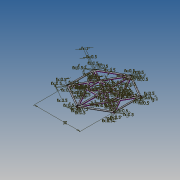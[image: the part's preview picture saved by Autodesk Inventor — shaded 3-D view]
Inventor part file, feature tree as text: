
AUTODESK INVENTOR PART (.ipt)
format: ipt  version: 2015 SP1 (Build 190203100, 203)  size: 1,105,920 bytes
history: native  units: mm
features: extrude x23, other x5, sketch x1, fillet x1, pattern_circular x1
ambient origin geometry x8: Origin, YZ Plane, XZ Plane, XY Plane, X Axis, Y Axis, Z Axis, Center Point
bodies: Solid1 (feature_tree), Solid3 (feature_tree), Solid4 (feature_tree), Solid5 (feature_tree), Solid6 (feature_tree), Solid7 (feature_tree), Solid8 (feature_tree), Solid9 (feature_tree), Solid11 (feature_tree), Solid12 (feature_tree), Solid13 (feature_tree), Solid14 (feature_tree), Solid16 (feature_tree), Solid17 (feature_tree), Solid18 (feature_tree), Solid19 (feature_tree), Solid20 (feature_tree), Solid21 (feature_tree), Solid22 (feature_tree), Solid23 (feature_tree), Solid24 (feature_tree), Solid25 (feature_tree), Solid26 (feature_tree), Solid27 (feature_tree), Solid28 (feature_tree), Solid29 (feature_tree), Solid30 (feature_tree), Solid31 (feature_tree)
feature tree (31):
  sketch  "Sketch1"  dims[d5=30.0mm d8=1.0mm d9=0.5mm d10=0.5mm d11=0.5mm d16=1.0mm d17=0.0mm d20=0.49mm d21=60.0mm d22=360.0deg d25=0.5mm d26=0.5mm d27=1.0mm d28=0.5mm d29=0.5mm d30=0.5mm d31=1.0mm d32=0.5mm d33=1.0mm d34=0.0mm d35=1.0mm d36=0.0mm d38=0.5mm d39=1.0mm d40=0.5mm d41=0.5mm d42=1.0mm d44=0.5mm d45=0.5mm d46=0.5mm d47=0.5mm d48=0.5mm d49=0.5mm d50=0.5mm d51=0.5mm d52=0.5mm d53=0.5mm d54=1.0mm d55=0.0mm d56=1.0mm d57=0.0mm d58=1.0mm d59=0.0mm d60=1.0mm d61=0.0mm d62=0.5mm d63=1.0mm d64=0.5mm d65=0.5mm d66=1.0mm d67=0.0mm d68=0.5mm d69=1.0mm d70=0.5mm d71=0.5mm d72=0.5mm d73=1.0mm d74=0.5mm d75=0.5mm d76=0.5mm d79=0.5mm d81=0.5mm d82=1.0mm d83=0.5mm d84=1.0mm d85=0.0mm d86=1.0mm d87=0.0mm d88=1.0mm d89=0.0mm d90=1.0mm d91=0.0mm d92=0.5mm d93=0.5mm d94=0.5mm d95=1.0mm d96=1.0mm d97=0.0mm d98=0.5mm d99=0.5mm d100=1.0mm d101=0.5mm d102=0.5mm d103=1.0mm d104=0.5mm d105=0.5mm d106=0.5mm d107=1.0mm d108=0.5mm d109=0.5mm d110=0.5mm d111=0.5mm d112=0.5mm d113=1.0mm d114=0.5mm d116=1.0mm d117=0.5mm d118=0.5mm d119=0.5mm d120=0.5mm d121=1.0mm d122=0.5mm d123=0.5mm d124=0.5mm d125=1.0mm d126=0.5mm d127=0.5mm d128=0.5mm d129=1.0mm d130=0.5mm d131=1.0mm d132=0.0mm d133=1.0mm d134=0.0mm d135=1.0mm d136=0.0mm d137=1.0mm d138=0.0mm d139=1.0mm d140=0.0mm d141=1.0mm d142=0.0mm d143=1.0mm d144=0.0mm d145=0.5mm d146=0.5mm d147=1.0mm d148=0.5mm d149=0.5mm d150=0.5mm d151=1.0mm d152=0.5mm d153=0.5mm d154=1.0mm d155=0.0mm d156=1.0mm d157=0.0mm d158=0.5mm d159=0.5mm d160=1.0mm d161=0.5mm d162=0.5mm d163=1.0mm d164=0.0mm]
  extrude  "Extrusion1"  Depth=1.0mm
  extrude  "Extrusion3"  Depth=1.0mm
  extrude  "Extrusion4"  Depth=1.0mm
  extrude  "Extrusion5"  Depth=1.0mm
  extrude  "Extrusion6"  Depth=1.0mm
  extrude  "Extrusion7"  TaperAngle=0.0deg  [1 undecoded]
  extrude  "Extrusion8"  Depth=0.49mm
  extrude  "Extrusion9"  Depth=1.0mm TaperAngle=360.0deg
  extrude  "Extrusion10"  Depth=1.0mm
  extrude  "Extrusion11"  Depth=1.0mm
  extrude  "Extrusion12"  Depth=1.0mm
  extrude  "Extrusion13"  Depth=1.0mm
  extrude  "Extrusion14"  Depth=1.0mm
  extrude  "Extrusion15"  Depth=1.0mm
  extrude  "Extrusion16"  Depth=1.0mm
  extrude  "Extrusion17"  Depth=1.0mm
  extrude  "Extrusion18"  Depth=1.0mm
  extrude  "Extrusion19"  TaperAngle=0.0deg  [1 undecoded]
  extrude  "Extrusion20"  Depth=1.0mm
  extrude  "Extrusion21"  TaperAngle=0.0deg  [1 undecoded]
  extrude  "Extrusion22"  Depth=1.0mm
  extrude  "Extrusion23"  Depth=1.0mm
  extrude  "Extrusion24"  Depth=1.0mm
  fillet  "Fillet1"  Radius=0.5mm
  pattern_circular  "Circular Pattern1"  [2 undecoded]
  other  "Pattern of Solid1:1"
  other  "Pattern of Solid1:2"
  other  "Pattern of Solid1:3"
  other  "Pattern of Solid1:4"
  other  "Pattern of Solid1:5"
note: 5 required parameter values undecoded (feature->parameter linkage not recoverable at this tier; creation-order binding heuristic only, values carry confidence <= 0.55)
